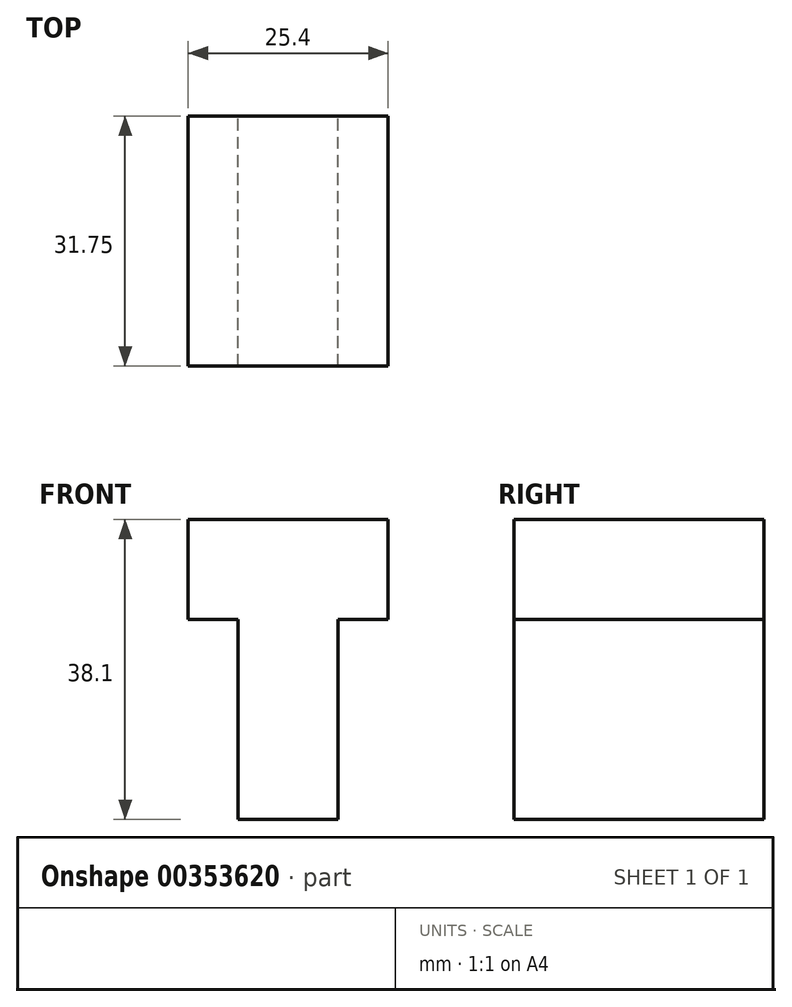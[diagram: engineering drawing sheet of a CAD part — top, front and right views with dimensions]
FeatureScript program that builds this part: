
annotation { "Feature Type Name" : "Feature", "Feature Type Description" : "" }
export const myFeature = defineFeature(function(context is Context, id is Id, definition is map)
    precondition{}
    {
        {
            var Q0;
            Q0=qCreatedBy(makeId("Front.planeOp"),FACE);
            var sketch = newSketch(context, id + "F0", { "sketchPlane" : qUnion([Q0])});
            skLineSegment(sketch, "E0", {"start": v(5.44, 0) * mm, "end": v(18.14, 0) * mm});
            skLineSegment(sketch, "E1", {"start": v(18.14, 0) * mm, "end": v(18.14, 25.4) * mm});
            skLineSegment(sketch, "E2", {"start": v(18.14, 25.4) * mm, "end": v(24.5, 25.4) * mm});
            skLineSegment(sketch, "E3", {"start": v(24.5, 25.4) * mm, "end": v(24.5, 38.1) * mm});
            skLineSegment(sketch, "E4", {"start": v(24.5, 38.1) * mm, "end": v(-0.9, 38.1) * mm});
            skLineSegment(sketch, "E5", {"start": v(-0.9, 38.1) * mm, "end": v(-0.9, 25.4) * mm});
            skLineSegment(sketch, "E6", {"start": v(-0.9, 25.4) * mm, "end": v(5.44, 25.4) * mm});
            skLineSegment(sketch, "E7", {"start": v(5.44, 25.4) * mm, "end": v(5.44, 0) * mm});
            skSolve(sketch);
        }
        {
            var Q0;
            Q0 = qSketchRegion(id + "F0", true);
            extrude(context, id + "F1", {"entities" : qUnion([Q0]), "depth" : 31.75 * mm});
        }
    });
